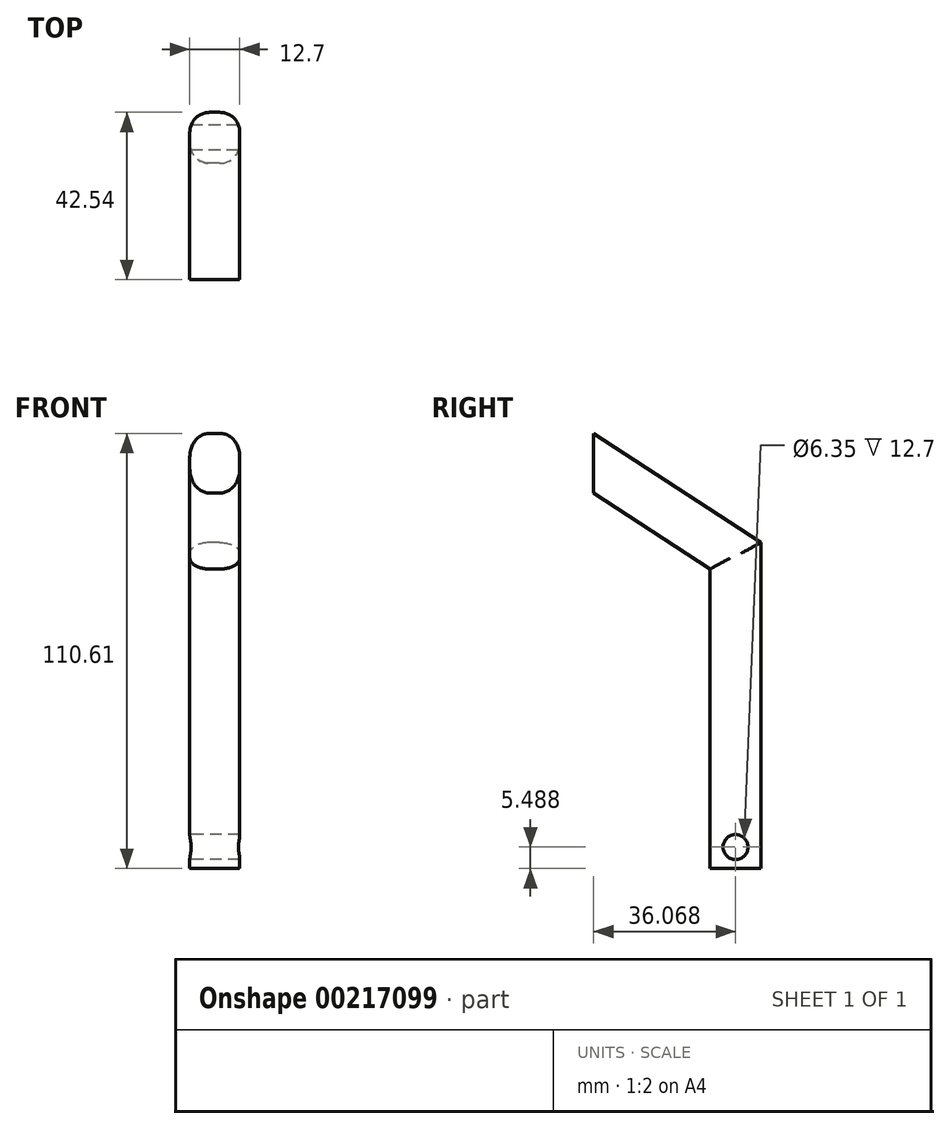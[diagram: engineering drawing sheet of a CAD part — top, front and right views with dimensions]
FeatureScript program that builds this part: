
annotation { "Feature Type Name" : "Feature", "Feature Type Description" : "" }
export const myFeature = defineFeature(function(context is Context, id is Id, definition is map)
    precondition{}
    {
        {
            var Q0;
            Q0=qCreatedBy(makeId("Right.planeOp"),FACE);
            var sketch = newSketch(context, id + "F0", { "sketchPlane" : qUnion([Q0])});
            skLineSegment(sketch, "E0", {"start": v(0, 18.75) * mm, "end": v(0, 101.6) * mm});
            skLineSegment(sketch, "E1", {"start": v(0, 101.6) * mm, "end": v(-42.54, 129.36) * mm});
            skLineSegment(sketch, "E2", {"start": v(-42.54, 129.36) * mm, "end": v(-49.48, 118.72) * mm});
            skLineSegment(sketch, "E3", {"start": v(-49.48, 118.72) * mm, "end": v(-12.94, 94.88) * mm});
            skLineSegment(sketch, "E4", {"start": v(-12.94, 94.88) * mm, "end": v(-12.94, 18.75) * mm});
            skCircle(sketch, "E5", {"center": v(-6.47, 24.24) * mm, "radius": 3.18 * mm});
            skPoint(sketch, "E5.centerSnap0", {"position": v(-6.47, 0) * mm});
            skLineSegment(sketch, "E6", {"start": v(-12.94, 14.92) * mm, "end": v(-14.12, 14.92) * mm});
            skLineSegment(sketch, "E7", {"start": v(0, 18.75) * mm, "end": v(-14.62, 18.75) * mm});
            skPoint(sketch, "E8.orphan", {"position": v(-12.94, 0) * mm});
            skPoint(sketch, "E9.end.orphan", {"position": v(0, 0) * mm});
            skSolve(sketch);
        }
        {
            var Q0;
            Q0=makeQuery(id+"F0.imprint","IMPRINT",FACE,{"disambiguationData":[TD([[makeQuery(id+"F0.imprint","IMPRINT",EDGE,{"derivedFrom":sQuery(id+"F0.wireOp",EDGE,"E0")}),1.0]])]});
            extrude(context, id + "F1", {"entities" : qUnion([Q0]), "depth" : 12.7 * mm});
        }
        {
            var Q0;
            Q0=makeQuery(id+"F1.opExtrude","CAP_FACE",FACE,{"disambiguationData":[OSD([sQuery(id+"F0.wireOp",EDGE,"E0"),sQuery(id+"F0.wireOp",EDGE,"E1"),sQuery(id+"F0.wireOp",EDGE,"E2"),sQuery(id+"F0.wireOp",EDGE,"E3"),sQuery(id+"F0.wireOp",EDGE,"E4"),sQuery(id+"F0.wireOp",EDGE,"E9"),sQuery(id+"F0.wireOp",EDGE,"E5")])],"isStart":true});
            var sketch = newSketch(context, id + "F2", { "sketchPlane" : qUnion([Q0])});
            skLineSegment(sketch, "E10", {"start": v(42.54, 129.36) * mm, "end": v(42.54, 114.2) * mm});
            skSolve(sketch);
        }
        {
            var Q0;
            {var subQ0=sQuery(id+"F2.wireOp",EDGE,"E10");Q0=makeQuery(id+"F2.imprint","IMPRINT",FACE,{"disambiguationData":[TD([[makeQuery(id+"F2.imprint","IMPRINT",EDGE,{"derivedFrom":subQ0}),1.0]])]});}
            extrude(context, id + "F3", {"entities" : qUnion([Q0]), "operationType" : NewBodyOperationType.REMOVE, "endBound" : BoundingType.THROUGH_ALL, "oppositeDirection" : true, "depth" : 25.4 * mm});
        }
        {
            var Q0;
            Q0=makeQuery(id+"F1.opExtrude","CAP_EDGE",EDGE,{"disambiguationData":[OSD([sQuery(id+"F0.wireOp",EDGE,"E4")])],"isStart":true});
            var Q1;
            Q1=makeQuery(id+"F1.opExtrude","CAP_EDGE",EDGE,{"disambiguationData":[OSD([sQuery(id+"F0.wireOp",EDGE,"E0")])],"isStart":true});
            var Q2;
            Q2=makeQuery(id+"F1.opExtrude","CAP_EDGE",EDGE,{"disambiguationData":[OSD([sQuery(id+"F0.wireOp",EDGE,"E4")])],"isStart":false});
            var Q3;
            Q3=makeQuery(id+"F1.opExtrude","CAP_EDGE",EDGE,{"disambiguationData":[OSD([sQuery(id+"F0.wireOp",EDGE,"E0")])],"isStart":false});
            var Q4;
            Q4=makeQuery(id+"F1.opExtrude","CAP_EDGE",EDGE,{"disambiguationData":[OSD([sQuery(id+"F0.wireOp",EDGE,"E3")])],"isStart":false});
            var Q5;
            Q5=makeQuery(id+"F1.opExtrude","CAP_EDGE",EDGE,{"disambiguationData":[OSD([sQuery(id+"F0.wireOp",EDGE,"E1")])],"isStart":false});
            var Q6;
            Q6=makeQuery(id+"F1.opExtrude","CAP_EDGE",EDGE,{"disambiguationData":[OSD([sQuery(id+"F0.wireOp",EDGE,"E1")])],"isStart":true});
            var Q7;
            Q7=makeQuery(id+"F1.opExtrude","CAP_EDGE",EDGE,{"disambiguationData":[OSD([sQuery(id+"F0.wireOp",EDGE,"E3")])],"isStart":true});
            fillet(context, id + "F4", {"entities" : qUnion([Q0, Q1, Q2, Q3, Q4, Q5, Q6, Q7]), "radius" : 5.08 * mm, "tangentPropagation" : true, "allowEdgeOverflow" : false});
        }
    });
